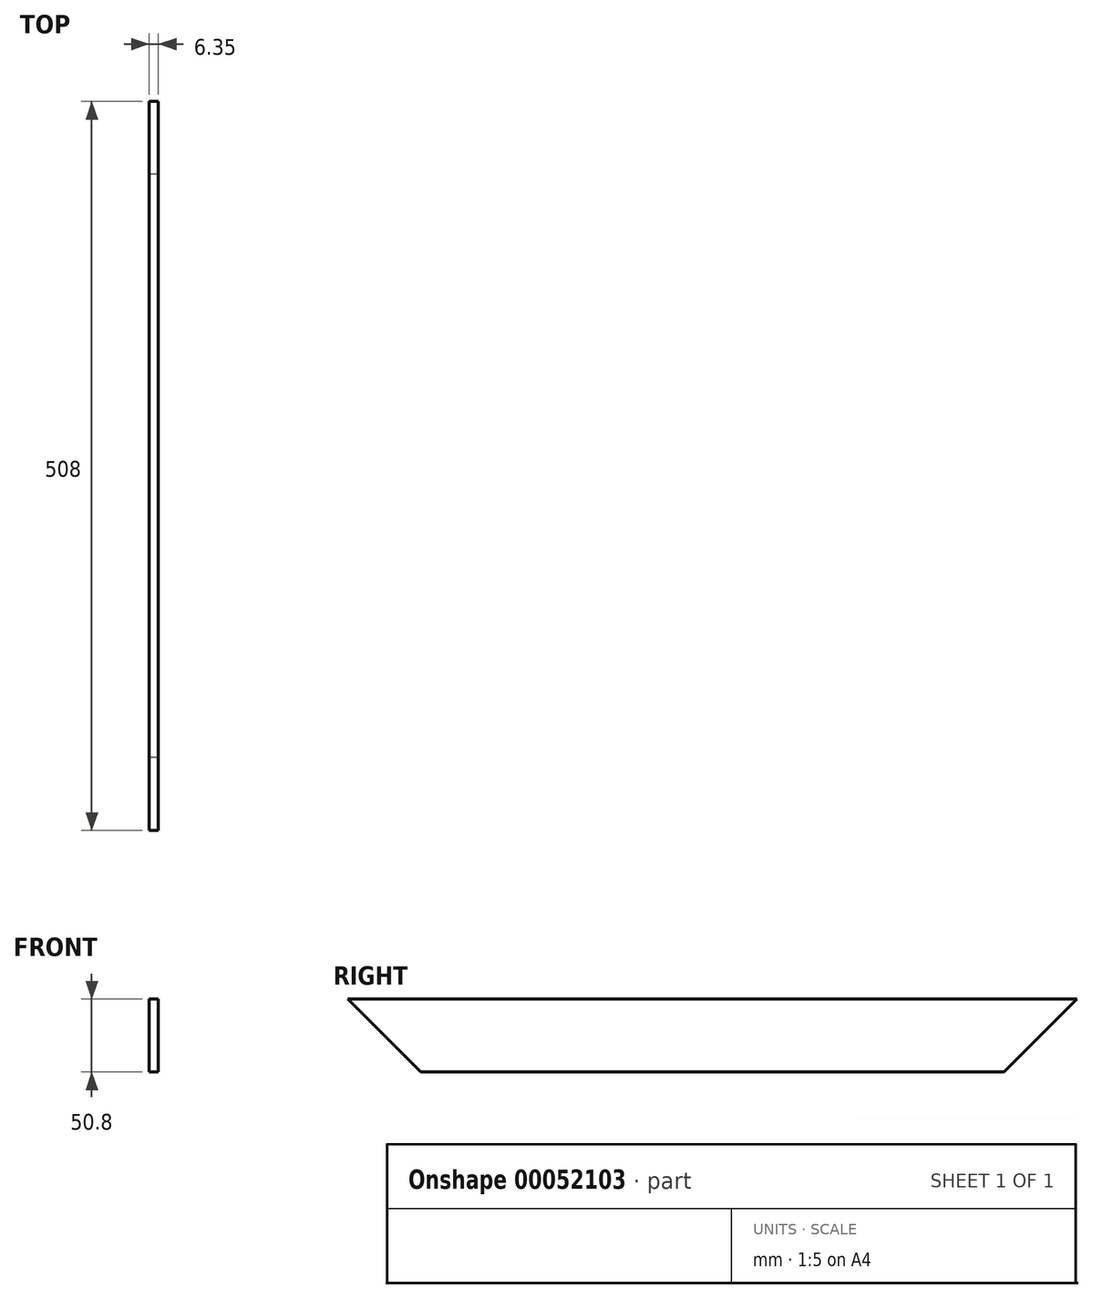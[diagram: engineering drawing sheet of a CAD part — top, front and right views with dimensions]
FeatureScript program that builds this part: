
annotation { "Feature Type Name" : "Feature", "Feature Type Description" : "" }
export const myFeature = defineFeature(function(context is Context, id is Id, definition is map)
    precondition{}
    {
        {
            var Q0;
            Q0=qCreatedBy(makeId("Right.planeOp"),FACE);
            var sketch = newSketch(context, id + "F0", { "sketchPlane" : qUnion([Q0])});
            skLineSegment(sketch, "E0", {"start": v(-203.2, 0) * mm, "end": v(203.2, 0) * mm});
            skLineSegment(sketch, "E1", {"start": v(203.2, 0) * mm, "end": v(254, 50.8) * mm});
            skLineSegment(sketch, "E2", {"start": v(254, 50.8) * mm, "end": v(0, 50.8) * mm});
            skLineSegment(sketch, "E3", {"start": v(0, 0) * mm, "end": v(0, 87.2) * mm, "construction": true});
            skLineSegment(sketch, "E4.MirrorCS", {"start": v(-254, 50.8) * mm, "end": v(0, 50.8) * mm});
            skLineSegment(sketch, "E5.MirrorCS", {"start": v(-203.2, 0) * mm, "end": v(-254, 50.8) * mm});
            skSolve(sketch);
        }
        {
            var Q0;
            Q0 = qSketchRegion(id + "F0", true);
            extrude(context, id + "F1", {"entities" : qUnion([Q0]), "depth" : 6.35 * mm});
        }
    });
